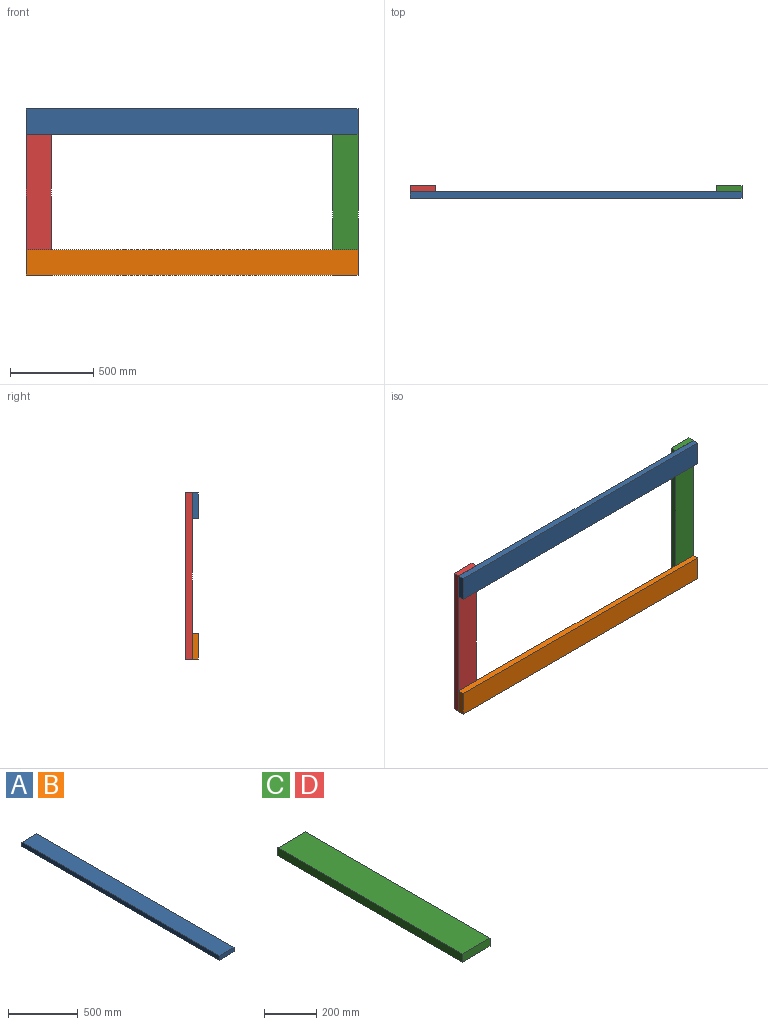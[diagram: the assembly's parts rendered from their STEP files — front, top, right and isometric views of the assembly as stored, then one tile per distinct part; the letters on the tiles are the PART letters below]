
ASSEMBLY  parts=4 mates=9
PART A: 6 faces, bbox 152x2000x38 mm
  f0: plane 2000x152mm, normal (0,0,-1), area 304000mm2, adj f1,f3,f4,f5
  f1: plane 2000x38mm, normal (1,0,0), area 76000mm2, adj f0,f2,f4,f5
  f2: plane 2000x152mm, normal (0,0,1), area 304000mm2, adj f1,f3,f4,f5
  f3: plane 2000x38mm, normal (-1,0,0), area 76000mm2, adj f0,f2,f4,f5
  f4: plane 152x38mm, normal (0,-1,0), area 5776mm2, adj f0,f1,f2,f3
  f5: plane 152x38mm, normal (0,1,0), area 5776mm2, adj f0,f1,f2,f3
PART B: same geometry as A
PART C: 6 faces, bbox 152x1000x38 mm
  f0: plane 1000x152mm, normal (0,0,-1), area 152000mm2, adj f1,f3,f4,f5
  f1: plane 1000x38mm, normal (1,0,0), area 38000mm2, adj f0,f2,f4,f5
  f2: plane 1000x152mm, normal (0,0,1), area 152000mm2, adj f1,f3,f4,f5
  f3: plane 1000x38mm, normal (-1,0,0), area 38000mm2, adj f0,f2,f4,f5
  f4: plane 152x38mm, normal (0,-1,0), area 5776mm2, adj f0,f1,f2,f3
  f5: plane 152x38mm, normal (0,1,0), area 5776mm2, adj f0,f1,f2,f3
PART D: same geometry as C
PLACE A rot(axis=(0.58,0.58,-0.58),120deg) t=(1600.54,-655.12,-104.94)mm
PLACE B rot(axis=(0.58,0.58,-0.58),120deg) t=(1600.54,-655.12,-952.94)mm
PLACE C rot(axis=(1,0,0),90deg) t=(2524.54,-617.12,-528.94)mm
PLACE D rot(axis=(1,0,0),90deg) t=(676.54,-617.12,-528.94)mm
MATE planar D.f2 <-> A.f0  axis (0,-1,0) through (676.54,-636.12,-528.94)mm
MATE planar A.f5 <-> B.f5  axis (1,0,0) through (2600.54,-655.12,-28.94)mm
MATE planar B.f2 <-> A.f2  axis (0,-1,0) through (1600.54,-674.12,-952.94)mm
MATE planar D.f5 <-> A.f3  axis (0,0,1) through (600.54,-598.12,-28.94)mm
MATE planar C.f2 <-> A.f0  axis (0,-1,0) through (2524.54,-636.12,-528.94)mm
MATE planar D.f3 <-> A.f4  axis (-1,0,0) through (600.54,-617.12,-528.94)mm
MATE planar B.f1 <-> D.f4  axis (0,0,-1) through (1600.54,-655.12,-1028.94)mm
MATE planar A.f3 <-> C.f5  axis (0,0,1) through (1600.54,-655.12,-28.94)mm
MATE planar C.f1 <-> A.f5  axis (1,0,0) through (2600.54,-617.12,-528.94)mm
